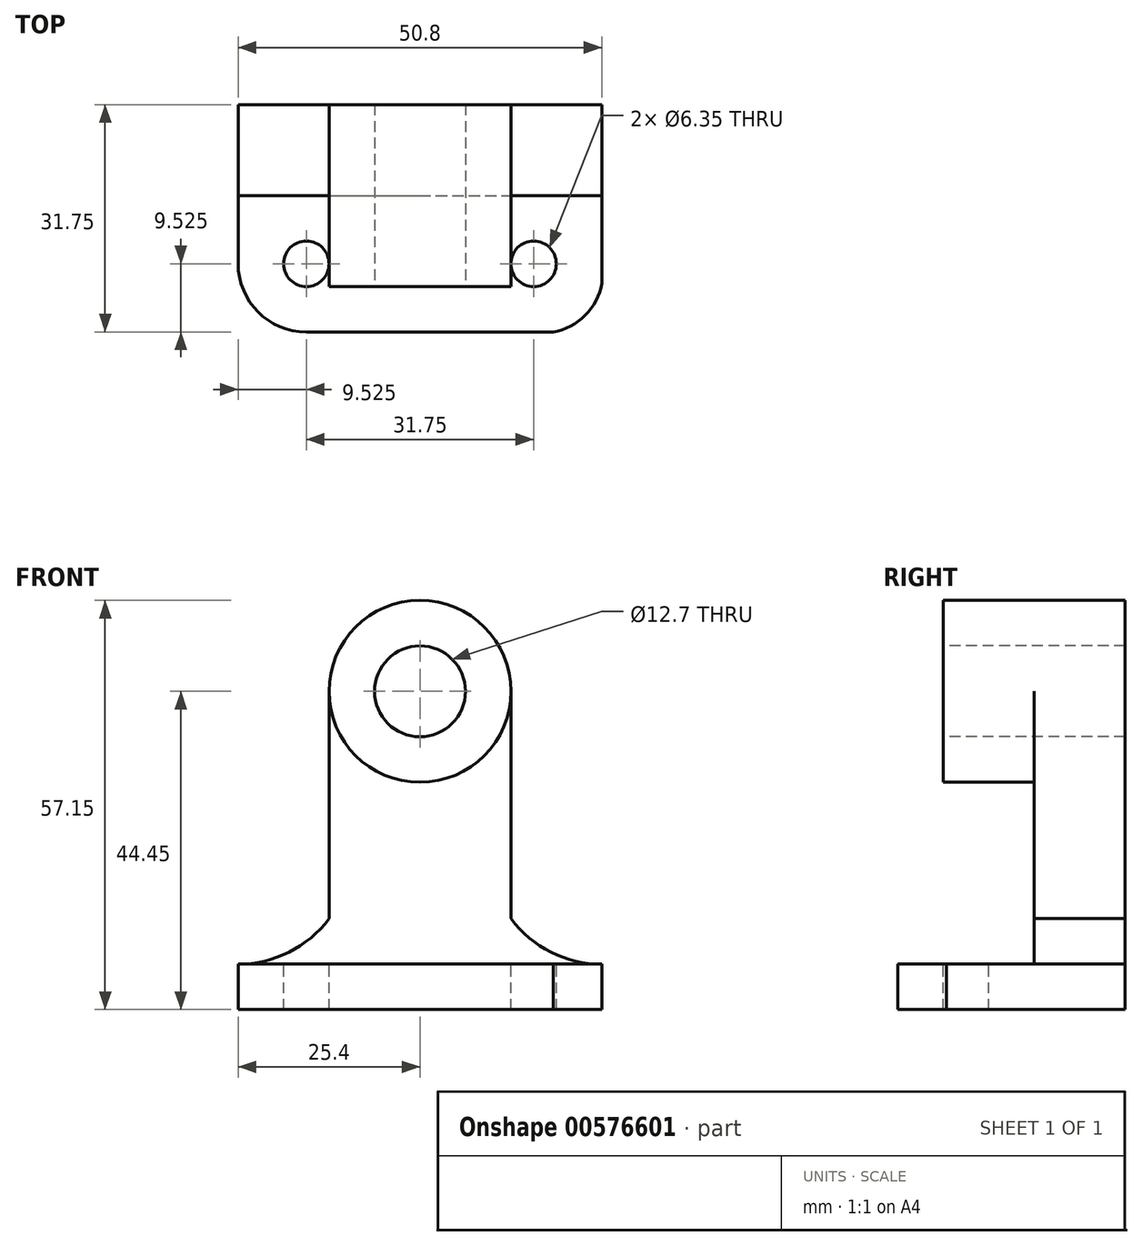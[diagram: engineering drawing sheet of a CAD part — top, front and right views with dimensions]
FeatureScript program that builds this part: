
annotation { "Feature Type Name" : "Feature", "Feature Type Description" : "" }
export const myFeature = defineFeature(function(context is Context, id is Id, definition is map)
    precondition{}
    {
        {
            var Q0;
            Q0=qCreatedBy(makeId("Top.planeOp"),FACE);
            var sketch = newSketch(context, id + "F0", { "sketchPlane" : qUnion([Q0])});
            skLineSegment(sketch, "E0", {"start": v(0, 0) * mm, "end": v(50.8, 0) * mm});
            skPoint(sketch, "E1.start.orphan", {"position": v(0, 36.84) * mm});
            skLineSegment(sketch, "E2", {"start": v(0, 0) * mm, "end": v(0, 31.75) * mm});
            skLineSegment(sketch, "E3", {"start": v(0, 31.75) * mm, "end": v(50.8, 31.75) * mm});
            skLineSegment(sketch, "E4", {"start": v(50.8, 0) * mm, "end": v(50.8, 31.75) * mm});
            skSolve(sketch);
        }
        {
            var Q0;
            Q0=makeQuery(id+"F0.imprint","IMPRINT",FACE,{"disambiguationData":[TD([[makeQuery(id+"F0.imprint","IMPRINT",EDGE,{"derivedFrom":sQuery(id+"F0.wireOp",EDGE,"E0")}),1.0]])]});
            extrude(context, id + "F1", {"entities" : qUnion([Q0]), "depth" : 6.35 * mm, "offsetDistance" : 25.4 * mm});
        }
        {
            var Q0;
            Q0=makeQuery(id+"F1.opExtrude","CAP_FACE",FACE,{"disambiguationData":[OSD([sQuery(id+"F0.wireOp",EDGE,"E0"),sQuery(id+"F0.wireOp",EDGE,"E2"),sQuery(id+"F0.wireOp",EDGE,"E3"),sQuery(id+"F0.wireOp",EDGE,"E4")])],"isStart":false});
            var sketch = newSketch(context, id + "F2", { "sketchPlane" : qUnion([Q0])});
            skCircle(sketch, "E5", {"center": v(9.53, 9.53) * mm, "radius": 3.18 * mm});
            skCircle(sketch, "E6", {"center": v(41.28, 9.53) * mm, "radius": 3.18 * mm});
            skArc(sketch, "E7", {"start": v(0, 9.52) * mm, "mid": v(2.79, 2.79) * mm, "end": v(9.52, 0) * mm});
            skArc(sketch, "E8", {"start": v(41.28, 0) * mm, "mid": v(48.49, 2.31) * mm, "end": v(50.8, 9.53) * mm});
            skSolve(sketch);
        }
        {
            var Q0;
            {var subQ0=sQuery(id+"F2.wireOp",EDGE,"E7");Q0=makeQuery(id+"F2.imprint","IMPRINT",FACE,{"disambiguationData":[TD([[makeQuery(id+"F2.imprint","IMPRINT",EDGE,{"derivedFrom":subQ0}),-1.0]])]});}
            var Q1;
            Q1=makeQuery(id+"F2.imprint","IMPRINT",FACE,{"disambiguationData":[TD([[makeQuery(id+"F2.imprint","IMPRINT",EDGE,{"derivedFrom":sQuery(id+"F2.wireOp",EDGE,"E5")}),1.0]])]});
            var Q2;
            Q2=makeQuery(id+"F2.imprint","IMPRINT",FACE,{"disambiguationData":[TD([[makeQuery(id+"F2.imprint","IMPRINT",EDGE,{"derivedFrom":sQuery(id+"F2.wireOp",EDGE,"E6")}),1.0]])]});
            var Q3;
            {var subQ0=sQuery(id+"F2.wireOp",EDGE,"E8");var subQ1=makeQuery(id+"F1.opExtrude","CAP_EDGE",EDGE,{"disambiguationData":[OSD([sQuery(id+"F0.wireOp",EDGE,"E0")])],"isStart":false});var subQ2=makeQuery(id+"F2.imprint","INTERSECT",VERTEX,{"disambiguationData":[OD(1.0)],"derivedFrom":[subQ1,subQ0]});Q3=makeQuery(id+"F2.imprint","IMPRINT",FACE,{"disambiguationData":[TD([[makeQuery(id+"F2.imprint","IMPRINT",EDGE,{"disambiguationData":[TD([[subQ2,-1.0]])],"derivedFrom":subQ0}),-1.0]])]});}
            extrude(context, id + "F3", {"entities" : qUnion([Q0, Q1, Q2, Q3]), "operationType" : NewBodyOperationType.REMOVE, "oppositeDirection" : true, "depth" : 25.4 * mm, "offsetDistance" : 25.4 * mm});
        }
        {
            var Q0;
            Q0=makeQuery(id+"F1.opExtrude","SWEPT_FACE",FACE,{"disambiguationData":[OSD([sQuery(id+"F0.wireOp",EDGE,"E3")])]});
            var sketch = newSketch(context, id + "F4", { "sketchPlane" : qUnion([Q0])});
            skLineSegment(sketch, "E9", {"start": v(-50.8, 6.35) * mm, "end": v(-50.8, 57.15) * mm});
            skLineSegment(sketch, "E10", {"start": v(-50.8, 57.15) * mm, "end": v(0, 57.15) * mm});
            skLineSegment(sketch, "E11", {"start": v(0, 57.15) * mm, "end": v(0, 6.35) * mm});
            skSolve(sketch);
        }
        {
            var Q0;
            Q0=makeQuery(id+"F4.imprint","IMPRINT",FACE,{"disambiguationData":[TD([[makeQuery(id+"F4.imprint","IMPRINT",EDGE,{"derivedFrom":sQuery(id+"F4.wireOp",EDGE,"E9")}),-1.0]])]});
            extrude(context, id + "F5", {"entities" : qUnion([Q0]), "oppositeDirection" : true, "depth" : 25.4 * mm, "offsetDistance" : 25.4 * mm});
        }
        {
            var Q0;
            Q0=makeQuery(id+"F5.opExtrude","CAP_FACE",FACE,{"disambiguationData":[OSD([sQuery(id+"F0.wireOp",EDGE,"E3"),sQuery(id+"F4.wireOp",EDGE,"E9"),sQuery(id+"F4.wireOp",EDGE,"E10"),sQuery(id+"F4.wireOp",EDGE,"E11")])],"isStart":false});
            var sketch = newSketch(context, id + "F6", { "sketchPlane" : qUnion([Q0])});
            skCircle(sketch, "E12", {"center": v(25.4, 44.45) * mm, "radius": 12.7 * mm});
            skLineSegment(sketch, "E13", {"start": v(38.1, 44.45) * mm, "end": v(38.1, 12.7) * mm});
            skArc(sketch, "E14", {"start": v(38.1, 12.7) * mm, "mid": v(43.7, 8.03) * mm, "end": v(50.8, 6.35) * mm});
            skLineSegment(sketch, "E15", {"start": v(12.7, 44.45) * mm, "end": v(12.7, 12.7) * mm});
            skArc(sketch, "E16", {"start": v(0, 6.35) * mm, "mid": v(7.1, 8.03) * mm, "end": v(12.7, 12.7) * mm});
            skSolve(sketch);
        }
        {
            var Q0;
            {var subQ1=sQuery(id+"F6.wireOp",EDGE,"E15");Q0=makeQuery(id+"F6.imprint","IMPRINT",FACE,{"disambiguationData":[TD([[makeQuery(id+"F6.imprint","IMPRINT",EDGE,{"derivedFrom":subQ1}),-1.0]])]});}
            var Q1;
            {var subQ1=sQuery(id+"F6.wireOp",EDGE,"E13");Q1=makeQuery(id+"F6.imprint","IMPRINT",FACE,{"disambiguationData":[TD([[makeQuery(id+"F6.imprint","IMPRINT",EDGE,{"derivedFrom":subQ1}),1.0]])]});}
            extrude(context, id + "F7", {"entities" : qUnion([Q0, Q1]), "operationType" : NewBodyOperationType.REMOVE, "oppositeDirection" : true, "depth" : 31.75 * mm, "offsetDistance" : 25.4 * mm});
        }
        {
            var Q0;
            Q0=makeQuery(id+"F5.opExtrude","CAP_FACE",FACE,{"disambiguationData":[OSD([sQuery(id+"F0.wireOp",EDGE,"E3"),sQuery(id+"F4.wireOp",EDGE,"E9"),sQuery(id+"F4.wireOp",EDGE,"E10"),sQuery(id+"F4.wireOp",EDGE,"E11")])],"isStart":false});
            var sketch = newSketch(context, id + "F8", { "sketchPlane" : qUnion([Q0])});
            skCircle(sketch, "E17", {"center": v(25.4, 44.45) * mm, "radius": 12.7 * mm});
            skSolve(sketch);
        }
        {
            var Q0;
            Q0=makeQuery(id+"F8.imprint","IMPRINT",FACE,{"disambiguationData":[TD([[makeQuery(id+"F8.imprint","IMPRINT",EDGE,{"derivedFrom":makeQuery(id+"F5.opExtrude","CAP_EDGE",EDGE,{"disambiguationData":[OSD([sQuery(id+"F0.wireOp",EDGE,"E3")])],"isStart":false})}),1.0]])]});
            extrude(context, id + "F9", {"entities" : qUnion([Q0]), "operationType" : NewBodyOperationType.REMOVE, "oppositeDirection" : true, "depth" : 12.7 * mm, "offsetDistance" : 25.4 * mm});
        }
        {
            var Q0;
            Q0=makeQuery(id+"F5.opExtrude","CAP_FACE",FACE,{"disambiguationData":[OSD([sQuery(id+"F0.wireOp",EDGE,"E3"),sQuery(id+"F4.wireOp",EDGE,"E9"),sQuery(id+"F4.wireOp",EDGE,"E10"),sQuery(id+"F4.wireOp",EDGE,"E11")])],"isStart":false});
            var sketch = newSketch(context, id + "F10", { "sketchPlane" : qUnion([Q0])});
            skCircle(sketch, "E18", {"center": v(25.4, 44.45) * mm, "radius": 6.35 * mm});
            skSolve(sketch);
        }
        {
            var Q0;
            Q0=makeQuery(id+"F10.imprint","IMPRINT",FACE,{"disambiguationData":[TD([[makeQuery(id+"F10.imprint","IMPRINT",EDGE,{"derivedFrom":sQuery(id+"F10.wireOp",EDGE,"E18")}),1.0]])]});
            extrude(context, id + "F11", {"entities" : qUnion([Q0]), "operationType" : NewBodyOperationType.REMOVE, "oppositeDirection" : true, "depth" : 25.4 * mm, "offsetDistance" : 25.4 * mm});
        }
    });
